# Revit family: Toilet-Elongated-American_Standard-Madera_Youth-2599.001.020
name_source: partatom
category: Plumbing Fixtures
units: mm (PartAtom-declared; Revit-internal decimal feet)

## family parameters
Always vertical = No
Cut with Voids When Loaded = No
OmniClass Number = 23.45.05.21.11
OmniClass Title = Water Closets
Part Type = Normal
Room Calculation Point = No
Round Connector Dimension = Use Radius
Shared = Yes
Work Plane-Based = Yes

## types (1)
- 2599.001.020
    10" Rough-In = Yes
    12" Rough-In = No
    ASME A112.18.1/CSA B125.1 = Yes
    Assembly Code = D2010110
    Bowl Shape = Elongated
    CW Connection = Yes
    CWFU = 10
    Cold Water Connection Diameter = 1"
    Cold Water Connection Height = 25 1/2"
    Cold Water Connection Radius = 1/2"
    Cold Water Connection Width = 4 3/4"
    Default Elevation = 0"
    Description = High Efficiency Madera Youth FloWise 14" Height Elongated Flushometer Toilet
    Finish = Vitreous China-American Standard-020-White
    Floor Flange Specification = Provide Floor Flange, (same material as the connecting pipe drain), with all brass bolts and with rubber gasket.
    Flush Rate = 1.28 to 1.6 gpf (4.8 Lpf to 6.0 Lpf)
    HW Connection = No
    HWFU = 0
    Height = 14"
    Installation Type = Floor Mounted
    Length = 28 1/4"
    Manufacturer = American Standard
    Material = Vitreous China-American Standard-020-White
    Model = 2599.001.020
    Price = Prices may vary. Please consult Manufacturer Representative for most up-to-date price list.
    Product Documentation Link = https://americanstandard.box.com
    Product Page URL = https://www.americanstandard-us.com
    Revised Date = 11/01/2021
    Rough-In Distance = 10"
    TAS(Texas Accessibility) = Yes
    URL = https://www.americanstandard-us.com
    Vent Connection = No
    WFU = 10
    Warranty Information = One Year Limited Warranty
    Waste Connection = Yes
    Waste Connection Diameter = 2 1/8"
    Waste Connection Radius = 1 1/16"
    Width = 14"

## geometry (parser evidence)
native form markers: Sweep x2
no freeform markers — native parametric forms only
